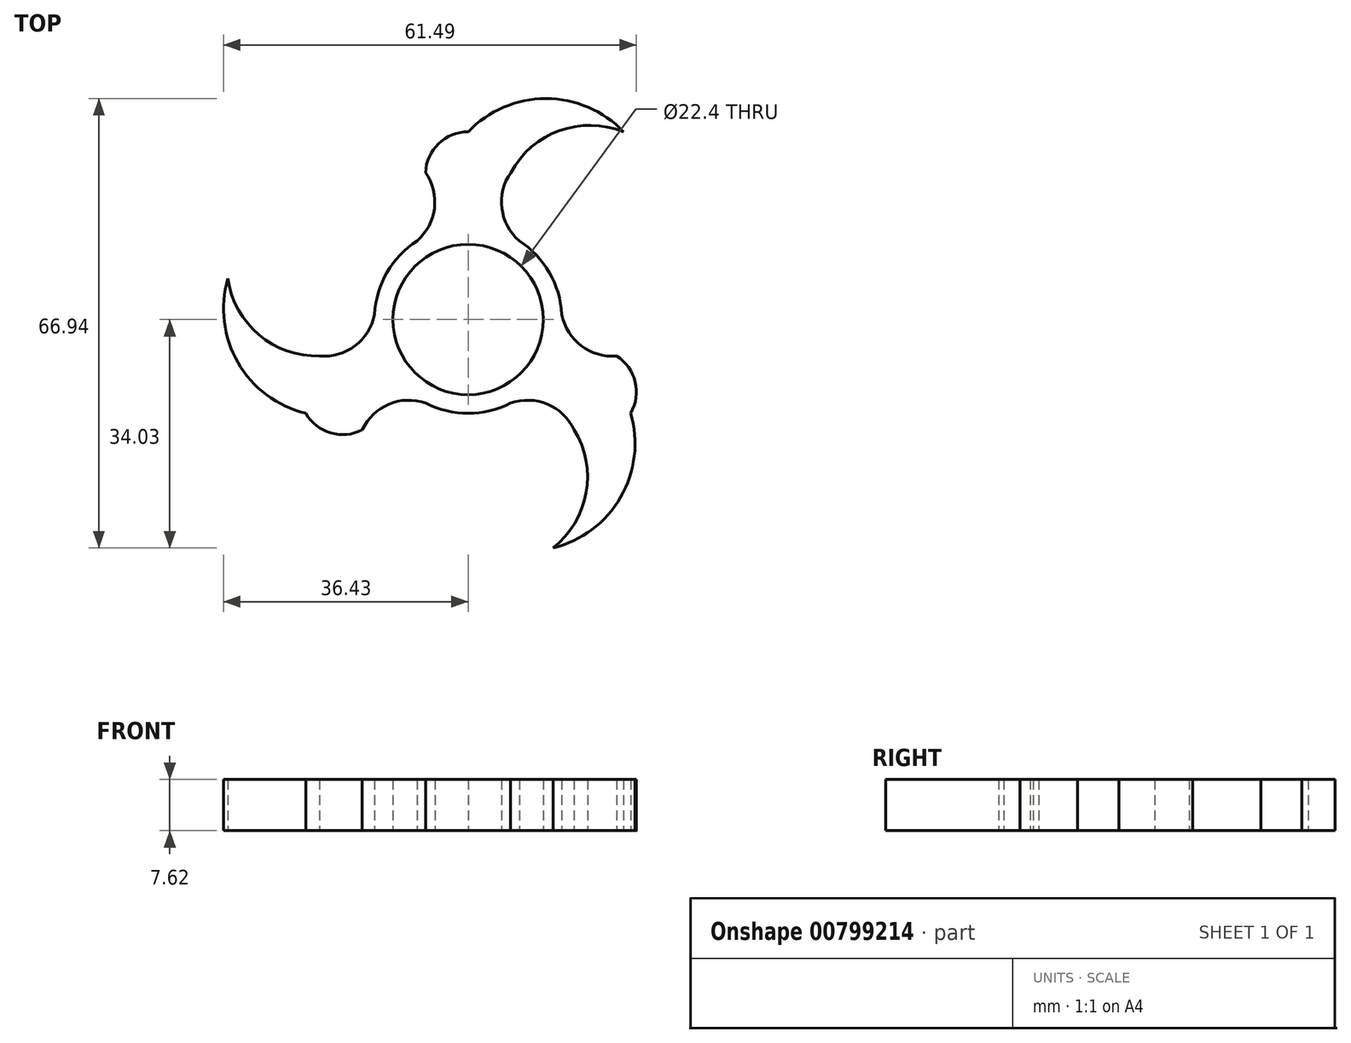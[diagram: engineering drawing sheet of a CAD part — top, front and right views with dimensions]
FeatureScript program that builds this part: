
annotation { "Feature Type Name" : "Feature", "Feature Type Description" : "" }
export const myFeature = defineFeature(function(context is Context, id is Id, definition is map)
    precondition{}
    {
        {
            var Q0;
            Q0=qCreatedBy(makeId("Top.planeOp"),FACE);
            var sketch = newSketch(context, id + "F0", { "sketchPlane" : qUnion([Q0])});
            skCircle(sketch, "E0", {"center": v(0, 0) * mm, "radius": 11.2 * mm});
            skCircle(sketch, "E1", {"center": v(0, 0) * mm, "radius": 13.97 * mm});
            skArc(sketch, "E2", {"start": v(-7.62, 11.7) * mm, "mid": v(-5.02, 16.54) * mm, "end": v(-6.35, 21.87) * mm});
            skArc(sketch, "E3", {"start": v(6.35, 21.87) * mm, "mid": v(5.02, 16.54) * mm, "end": v(7.62, 11.7) * mm});
            skArc(sketch, "E4", {"start": v(6.35, 21.87) * mm, "mid": v(0, 27.95) * mm, "end": v(-6.35, 21.87) * mm});
            skPoint(sketch, "E5.startSnap0", {"position": v(0, 27.95) * mm});
            skArc(sketch, "E6", {"start": v(23.16, 27.95) * mm, "mid": v(13.59, 28.12) * mm, "end": v(6.35, 21.87) * mm});
            skArc(sketch, "E7", {"start": v(23.16, 27.95) * mm, "mid": v(11.58, 32.9) * mm, "end": v(0, 27.95) * mm});
            skArc(sketch, "E8.1.0", {"start": v(-35.78, 6.08) * mm, "mid": v(-34.29, -6.43) * mm, "end": v(-24.2, -13.98) * mm});
            skArc(sketch, "E8.1.1", {"start": v(-6.33, -12.45) * mm, "mid": v(-11.82, -12.62) * mm, "end": v(-15.76, -16.43) * mm});
            skArc(sketch, "E8.1.2", {"start": v(-22.11, -5.44) * mm, "mid": v(-16.84, -3.92) * mm, "end": v(-13.95, 0.74) * mm});
            skArc(sketch, "E8.1.3", {"start": v(-35.78, 6.08) * mm, "mid": v(-31.15, -2.3) * mm, "end": v(-22.11, -5.44) * mm});
            skPoint(sketch, "E8.1.4", {"position": v(-24.2, -13.98) * mm});
            skArc(sketch, "E8.1.5", {"start": v(-22.11, -5.44) * mm, "mid": v(-24.2, -13.98) * mm, "end": v(-15.76, -16.43) * mm});
            skArc(sketch, "E8.2.0", {"start": v(12.63, -34.03) * mm, "mid": v(22.71, -26.48) * mm, "end": v(24.2, -13.98) * mm});
            skArc(sketch, "E8.2.1", {"start": v(13.95, 0.74) * mm, "mid": v(16.84, -3.92) * mm, "end": v(22.11, -5.44) * mm});
            skArc(sketch, "E8.2.2", {"start": v(15.76, -16.43) * mm, "mid": v(11.82, -12.62) * mm, "end": v(6.33, -12.45) * mm});
            skArc(sketch, "E8.2.3", {"start": v(12.63, -34.03) * mm, "mid": v(17.56, -25.83) * mm, "end": v(15.76, -16.43) * mm});
            skPoint(sketch, "E8.2.4", {"position": v(24.2, -13.98) * mm});
            skArc(sketch, "E8.2.5", {"start": v(15.76, -16.43) * mm, "mid": v(24.2, -13.98) * mm, "end": v(22.11, -5.44) * mm});
            skSolve(sketch);
        }
        {
            var Q0;
            {var subQ3=sQuery(id+"F0.wireOp",EDGE,"E8.1.1");Q0=makeQuery(id+"F0.imprint","IMPRINT",FACE,{"disambiguationData":[TD([[makeQuery(id+"F0.imprint","IMPRINT",EDGE,{"derivedFrom":subQ3}),-1.0]])]});}
            var Q1;
            {var subQ0=sQuery(id+"F0.wireOp",EDGE,"E8.1.0");Q1=makeQuery(id+"F0.imprint","IMPRINT",FACE,{"disambiguationData":[TD([[makeQuery(id+"F0.imprint","IMPRINT",EDGE,{"derivedFrom":subQ0}),1.0]])]});}
            var Q2;
            {var subQ3=sQuery(id+"F0.wireOp",EDGE,"E2");Q2=makeQuery(id+"F0.imprint","IMPRINT",FACE,{"disambiguationData":[TD([[makeQuery(id+"F0.imprint","IMPRINT",EDGE,{"derivedFrom":subQ3}),-1.0]])]});}
            var Q3;
            {var subQ0=sQuery(id+"F0.wireOp",EDGE,"E6");Q3=makeQuery(id+"F0.imprint","IMPRINT",FACE,{"disambiguationData":[TD([[makeQuery(id+"F0.imprint","IMPRINT",EDGE,{"derivedFrom":subQ0}),-1.0]])]});}
            var Q4;
            Q4=makeQuery(id+"F0.imprint","IMPRINT",FACE,{"disambiguationData":[TD([[makeQuery(id+"F0.imprint","IMPRINT",EDGE,{"derivedFrom":sQuery(id+"F0.wireOp",EDGE,"E0")}),-1.0]])]});
            var Q5;
            {var subQ3=sQuery(id+"F0.wireOp",EDGE,"E8.2.1");Q5=makeQuery(id+"F0.imprint","IMPRINT",FACE,{"disambiguationData":[TD([[makeQuery(id+"F0.imprint","IMPRINT",EDGE,{"derivedFrom":subQ3}),-1.0]])]});}
            var Q6;
            {var subQ0=sQuery(id+"F0.wireOp",EDGE,"E8.2.0");Q6=makeQuery(id+"F0.imprint","IMPRINT",FACE,{"disambiguationData":[TD([[makeQuery(id+"F0.imprint","IMPRINT",EDGE,{"derivedFrom":subQ0}),1.0]])]});}
            extrude(context, id + "F1", {"entities" : qUnion([Q0, Q1, Q2, Q3, Q4, Q5, Q6]), "depth" : 7.62 * mm, "offsetDistance" : 25.4 * mm});
        }
    });
